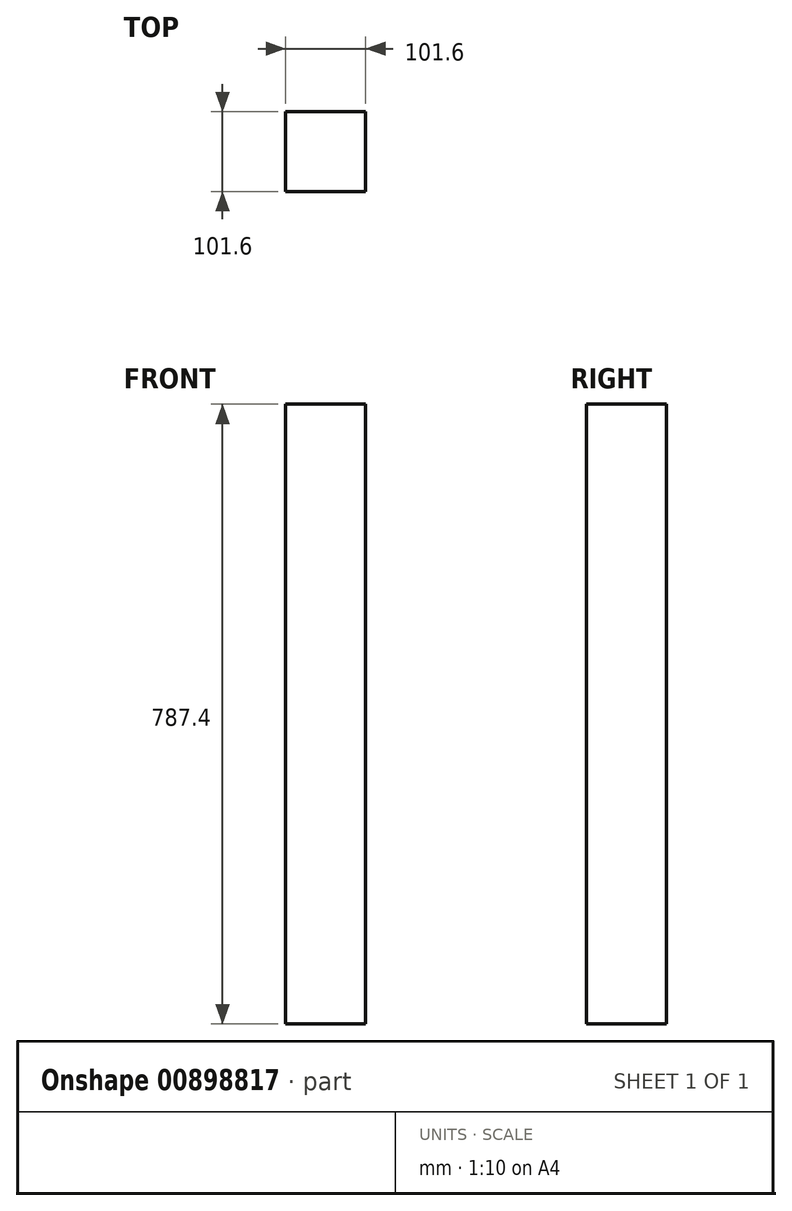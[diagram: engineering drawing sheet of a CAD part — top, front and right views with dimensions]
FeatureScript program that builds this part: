
annotation { "Feature Type Name" : "Feature", "Feature Type Description" : "" }
export const myFeature = defineFeature(function(context is Context, id is Id, definition is map)
    precondition{}
    {
        {
            var Q0;
            Q0=qCreatedBy(makeId("Top.planeOp"),FACE);
            var sketch = newSketch(context, id + "F0", { "sketchPlane" : qUnion([Q0])});
            skLineSegment(sketch, "E0.bottom", {"start": v(0, 0) * mm, "end": v(101.6, 0) * mm});
            skLineSegment(sketch, "E0.top", {"start": v(0, 101.6) * mm, "end": v(101.6, 101.6) * mm});
            skLineSegment(sketch, "E0.left", {"start": v(0, 0) * mm, "end": v(0, 101.6) * mm});
            skLineSegment(sketch, "E0.right", {"start": v(101.6, 0) * mm, "end": v(101.6, 101.6) * mm});
            skSolve(sketch);
        }
        {
            var Q0;
            Q0 = qSketchRegion(id + "F0", true);
            extrude(context, id + "F1", {"entities" : qUnion([Q0]), "depth" : 787.4 * mm, "offsetDistance" : 25.4 * mm});
        }
    });
